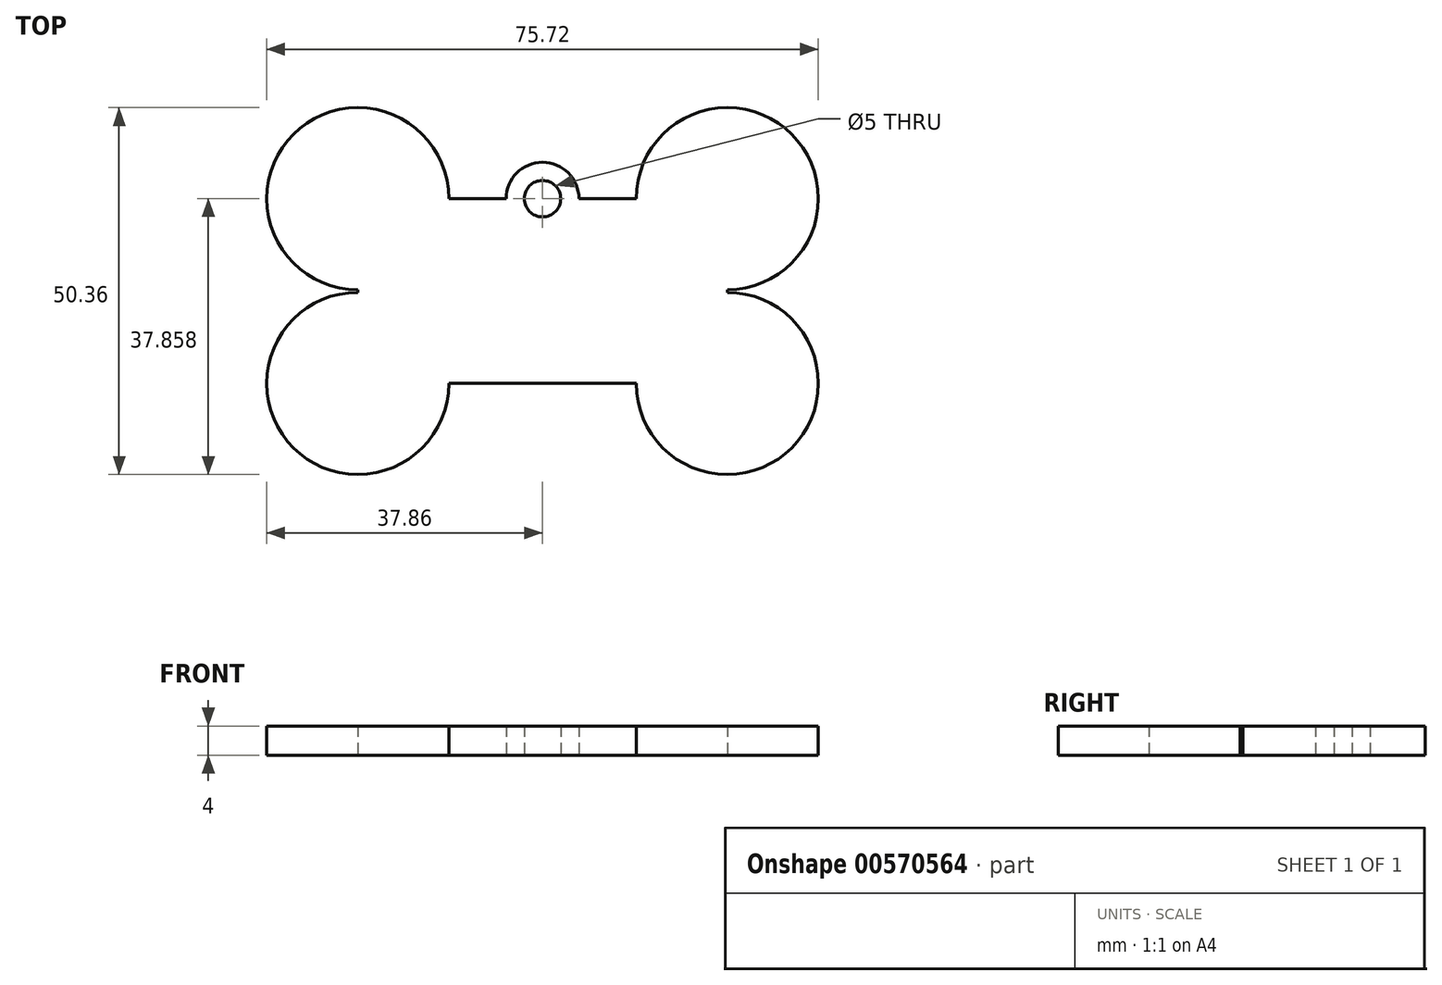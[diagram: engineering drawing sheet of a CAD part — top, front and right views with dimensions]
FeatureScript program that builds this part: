
annotation { "Feature Type Name" : "Feature", "Feature Type Description" : "" }
export const myFeature = defineFeature(function(context is Context, id is Id, definition is map)
    precondition{}
    {
        {
            var Q0;
            Q0=qCreatedBy(makeId("Top.planeOp"),FACE);
            var sketch = newSketch(context, id + "F0", { "sketchPlane" : qUnion([Q0])});
            skLineSegment(sketch, "E0.bottom", {"start": v(12.86, -12.68) * mm, "end": v(-12.86, -12.68) * mm});
            skLineSegment(sketch, "E0.top", {"start": v(12.86, 12.68) * mm, "end": v(5, 12.68) * mm});
            skLineSegment(sketch, "E0.left", {"start": v(25.36, -0.18) * mm, "end": v(25.36, 0.18) * mm});
            skLineSegment(sketch, "E0.right", {"start": v(-25.36, -0.18) * mm, "end": v(-25.36, 0.18) * mm});
            skPoint(sketch, "E0.middle", {"position": v(0, 0) * mm});
            skArc(sketch, "E1", {"start": v(25.36, 0.18) * mm, "mid": v(34.2, 21.52) * mm, "end": v(12.86, 12.68) * mm});
            skArc(sketch, "E2", {"start": v(12.86, -12.68) * mm, "mid": v(34.2, -21.52) * mm, "end": v(25.36, -0.18) * mm});
            skArc(sketch, "E3", {"start": v(-25.36, -0.18) * mm, "mid": v(-34.2, -21.52) * mm, "end": v(-12.86, -12.68) * mm});
            skArc(sketch, "E4", {"start": v(-12.86, 12.68) * mm, "mid": v(-34.2, 21.52) * mm, "end": v(-25.36, 0.18) * mm});
            skArc(sketch, "E5", {"start": v(5, 12.68) * mm, "mid": v(0, 17.68) * mm, "end": v(-5, 12.68) * mm});
            skLineSegment(sketch, "E6.trimOffspring", {"start": v(-5, 12.68) * mm, "end": v(-12.86, 12.68) * mm});
            skCircle(sketch, "E7", {"center": v(0, 12.68) * mm, "radius": 2.5 * mm});
            skSolve(sketch);
        }
        {
            var Q0;
            Q0=makeQuery(id+"F0.imprint","IMPRINT",FACE,{"disambiguationData":[TD([[makeQuery(id+"F0.imprint","IMPRINT",EDGE,{"derivedFrom":sQuery(id+"F0.wireOp",EDGE,"E0.bottom")}),-1.0]])]});
            extrude(context, id + "F1", {"entities" : qUnion([Q0]), "depth" : 4 * mm, "offsetDistance" : 25 * mm});
        }
    });
